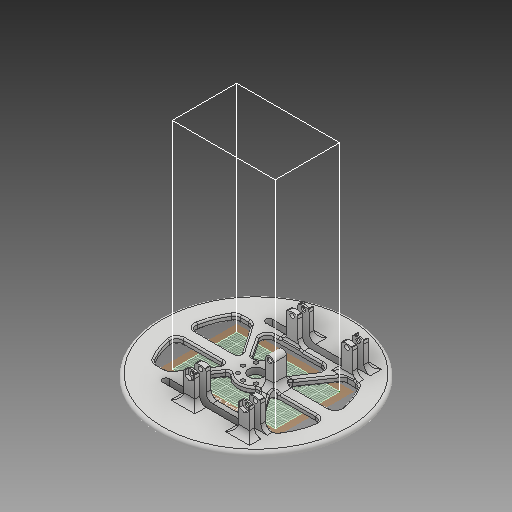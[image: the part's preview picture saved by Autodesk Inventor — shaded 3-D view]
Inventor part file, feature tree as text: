
AUTODESK INVENTOR PART (.ipt)
format: ipt  version: 2018 (Build 220112000, 112)  size: 1,802,752 bytes
history: native  units: mm
features: sketch x8, extrude x8, fillet x6, mirror x5, plane x2, projected_geometry x2, hole x1
ambient origin geometry x8: Origin, YZ Plane, XZ Plane, XY Plane, X Axis, Y Axis, Z Axis, Center Point
bodies: Solid1 (feature_tree)
feature tree (32):
  sketch  "Sketch1"  dims[d1=80.0mm d2=120.0mm d3=14.0mm d4=14.0mm d5=14.0mm d6=9.0mm d7=16.0mm d8=360.0deg d9=22.0mm d10=8.0mm d11=8.0mm d12=30.0mm d13=30.0mm d14=34.0mm d15=4.0mm d16=0.0mm]
  extrude  "Extrusion1"  Depth=4.0mm TaperAngle=0.0deg
  extrude  "Extrusion2"  Depth=8.0mm
  mirror  "Mirror1"
  hole  "Hole1"  [1 undecoded]
  extrude  "Extrusion3"  Depth=3.0mm TaperAngle=0.0deg
  mirror  "Mirror2"
  extrude  "Extrusion4"  Depth=5.2mm
  plane  "Work Plane1"
  mirror  "Mirror3"
  extrude  "Extrusion5"  Depth=2.0mm TaperAngle=0.0deg
  extrude  "Extrusion6"  Depth=0.3mm
  plane  "Work Plane2"
  mirror  "Mirror4"
  extrude  "Extrusion7"  Depth=2.0mm TaperAngle=0.0deg
  mirror  "Mirror5"
  fillet  "Fillet8"  Radius=4.0mm
  fillet  "Fillet9"  Radius=2.0mm
  fillet  "Fillet10"  Radius=4.0mm
  fillet  "Fillet11"  Radius=1.0mm
  fillet  "Fillet12"  Radius=6.0mm
  extrude  "Extrusion8"  Depth=2.0mm
  fillet  "Fillet13"  Radius=2.5mm
  sketch  "Sketch2"  dims[d17=4.0mm d18=0.0mm]
  sketch  "Sketch3"  dims[d19=2.5mm d20=6.0mm d21=4.0mm d22=2.0mm d23=90.0deg d24=8.0mm d25=20.594885mm d27=90.0mm]
  sketch  "Sketch4"  dims[d28=45.0mm d29=4.0mm]
  sketch  "Sketch5"  dims[d31=4.0mm d32=0.0mm]
  sketch  "Sketch6"  dims[d33=7.0mm d34=12.5mm d35=7.0mm d36=17.0mm d37=17.0mm d38=15.0mm d39=7.0mm d40=3.0mm d41=0.0mm]
  projected_geometry  "Projected Loop1"
  projected_geometry  "Projected Loop2"
  sketch  "Sketch7"  dims[d42=5.2mm d43=5.2mm]
  sketch  "Sketch8"  dims[d44=5.2mm d45=2.0mm d46=0.0mm d47=2.0mm d48=0.0mm d49=1.0mm d50=2.0mm d51=0.0mm d59=4.0mm d60=2.0mm d61=4.0mm d62=1.0mm d63=6.0mm d64=2.0mm d65=2.5mm d66=2.0mm d67=0.0mm d68=0.3mm]
note: 1 required parameter value undecoded (feature->parameter linkage not recoverable at this tier; creation-order binding heuristic only, values carry confidence <= 0.55)
